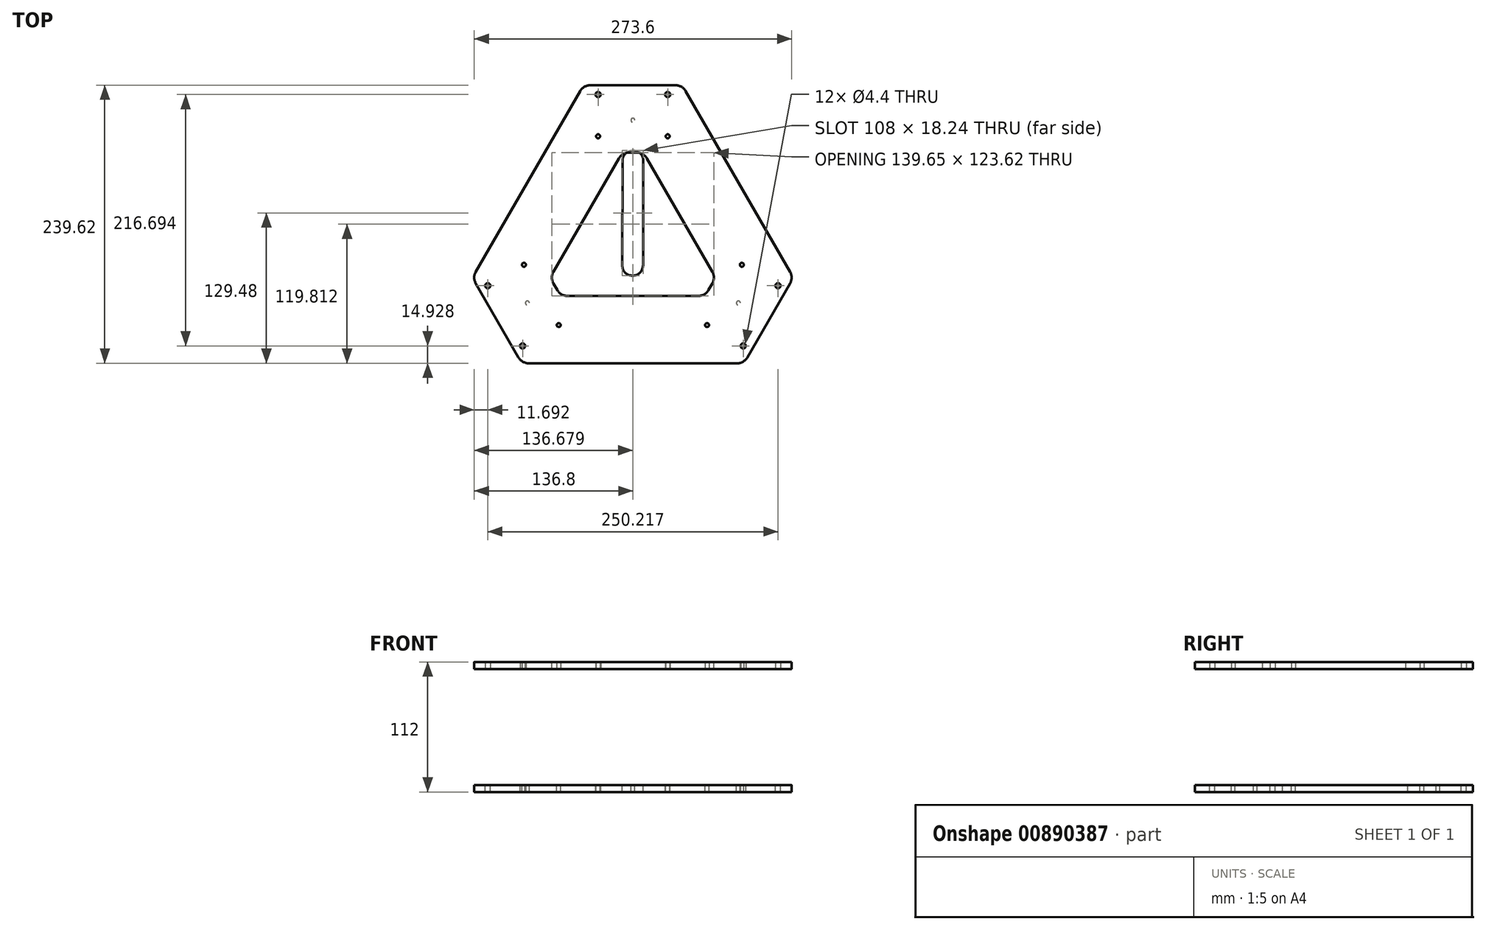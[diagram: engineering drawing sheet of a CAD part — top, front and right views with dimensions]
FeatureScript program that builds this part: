
annotation { "Feature Type Name" : "Feature", "Feature Type Description" : "" }
export const myFeature = defineFeature(function(context is Context, id is Id, definition is map)
    precondition{}
    {
        {
            var Q0;
            Q0=qCreatedBy(makeId("Top.planeOp"),FACE);
            var sketch = newSketch(context, id + "F0", { "sketchPlane" : qUnion([Q0])});
            skLineSegment(sketch, "E0", {"start": v(-138.35, -30.66) * mm, "end": v(-42.62, 135.14) * mm});
            skLineSegment(sketch, "E1", {"start": v(-42.62, 135.14) * mm, "end": v(42.62, 135.14) * mm});
            skLineSegment(sketch, "E2", {"start": v(42.62, 135.14) * mm, "end": v(138.34, -30.66) * mm});
            skLineSegment(sketch, "E3", {"start": v(138.34, -30.66) * mm, "end": v(95.73, -104.48) * mm});
            skLineSegment(sketch, "E4", {"start": v(95.73, -104.48) * mm, "end": v(-95.73, -104.48) * mm});
            skLineSegment(sketch, "E5", {"start": v(-95.73, -104.48) * mm, "end": v(-138.35, -30.66) * mm});
            skLineSegment(sketch, "E6", {"start": v(-90.48, 52.24) * mm, "end": v(0, 0) * mm, "construction": true});
            skLineSegment(sketch, "E7", {"start": v(0, -104.48) * mm, "end": v(0, 0) * mm, "construction": true});
            skLineSegment(sketch, "E8", {"start": v(90.48, 52.24) * mm, "end": v(0, 0) * mm, "construction": true});
            skPoint(sketch, "E9", {"position": v(0, 0) * mm});
            skLineSegment(sketch, "E10.0", {"start": v(62.24, -46.48) * mm, "end": v(-62.24, -46.48) * mm});
            skLineSegment(sketch, "E10.1", {"start": v(-71.37, -30.66) * mm, "end": v(-9.13, 77.14) * mm});
            skLineSegment(sketch, "E10.2", {"start": v(-9.13, 77.14) * mm, "end": v(9.13, 77.14) * mm});
            skLineSegment(sketch, "E10.3", {"start": v(-62.24, -46.48) * mm, "end": v(-71.37, -30.66) * mm});
            skLineSegment(sketch, "E10.4", {"start": v(9.13, 77.14) * mm, "end": v(71.37, -30.66) * mm});
            skLineSegment(sketch, "E10.5", {"start": v(71.37, -30.66) * mm, "end": v(62.24, -46.48) * mm});
            skCircle(sketch, "E11", {"center": v(95.1, -89.55) * mm, "radius": 2.2 * mm});
            skLineSegment(sketch, "E12", {"start": v(117.04, -67.57) * mm, "end": v(66.8, -38.57) * mm, "construction": true});
            skCircle(sketch, "E13", {"center": v(63.93, -71.55) * mm, "radius": 1.7 * mm});
            skCircle(sketch, "E14.MirrorC", {"center": v(93.93, -19.6) * mm, "radius": 1.7 * mm});
            skCircle(sketch, "E15.MirrorC", {"center": v(125.1, -37.6) * mm, "radius": 2.2 * mm});
            skLineSegment(sketch, "E16.0", {"start": v(95.1, -89.55) * mm, "end": v(95.1, -89.55) * mm});
            skLineSegment(sketch, "E16.1", {"start": v(95.1, -89.55) * mm, "end": v(63.93, -71.55) * mm, "construction": true});
            skCircle(sketch, "E17.1.0", {"center": v(-30, 91.14) * mm, "radius": 1.7 * mm});
            skCircle(sketch, "E17.1.1", {"center": v(-30, 127.14) * mm, "radius": 2.2 * mm});
            skCircle(sketch, "E17.1.2", {"center": v(30, 127.14) * mm, "radius": 2.2 * mm});
            skCircle(sketch, "E17.1.3", {"center": v(30, 91.14) * mm, "radius": 1.7 * mm});
            skCircle(sketch, "E17.2.0", {"center": v(-63.93, -71.55) * mm, "radius": 1.7 * mm});
            skCircle(sketch, "E17.2.1", {"center": v(-95.1, -89.55) * mm, "radius": 2.2 * mm});
            skCircle(sketch, "E17.2.2", {"center": v(-125.1, -37.6) * mm, "radius": 2.2 * mm});
            skCircle(sketch, "E17.2.3", {"center": v(-93.93, -19.6) * mm, "radius": 1.7 * mm});
            skSolve(sketch);
        }
        {
            var Q0;
            {var subQ0=sQuery(id+"F0.wireOp",EDGE,"vAaXFV3b-EpbO-ac0L-dCJ6-TkjUisyF59UN");Q0=makeQuery(id+"F0.imprint","IMPRINT",FACE,{"disambiguationData":[TD([[makeQuery(id+"F0.imprint","IMPRINT",EDGE,{"derivedFrom":subQ0}),1.0]])]});}
            var Q1;
            Q1=makeQuery(id+"F0.imprint","IMPRINT",FACE,{"disambiguationData":[TD([[makeQuery(id+"F0.imprint","IMPRINT",EDGE,{"derivedFrom":sQuery(id+"F0.wireOp",EDGE,"E0")}),-1.0]])]});
            extrude(context, id + "F1", {"entities" : qUnion([Q0, Q1]), "depth" : 6 * mm, "offsetDistance" : 25 * mm});
        }
        {
            var Q0;
            Q0=makeQuery(id+"F1.opExtrude","CAP_FACE",FACE,{"disambiguationData":[OSD([sQuery(id+"F0.wireOp",EDGE,"E0"),sQuery(id+"F0.wireOp",EDGE,"E1"),sQuery(id+"F0.wireOp",EDGE,"E2"),sQuery(id+"F0.wireOp",EDGE,"E3"),sQuery(id+"F0.wireOp",EDGE,"E4"),sQuery(id+"F0.wireOp",EDGE,"E5"),sQuery(id+"F0.wireOp",EDGE,"E10.0"),sQuery(id+"F0.wireOp",EDGE,"E10.1"),sQuery(id+"F0.wireOp",EDGE,"E10.2"),sQuery(id+"F0.wireOp",EDGE,"E10.3"),sQuery(id+"F0.wireOp",EDGE,"E10.4"),sQuery(id+"F0.wireOp",EDGE,"E10.5")])],"isStart":true});
            cPlane(context, id + "F2", {"entities" : qUnion([Q0]), "cplaneType" : CPlaneType.OFFSET, "offset" : 100 * mm, "width" : 150 * mm, "height" : 150 * mm});
        }
        {
            var Q0;
            Q0=qCreatedBy(id+"F2.planeOp",FACE);
            var sketch = newSketch(context, id + "F3", { "sketchPlane" : qUnion([Q0])});
            skLineSegment(sketch, "E18", {"start": v(-95.73, 104.48) * mm, "end": v(95.73, 104.48) * mm});
            skLineSegment(sketch, "E19", {"start": v(95.73, 104.48) * mm, "end": v(138.35, 30.66) * mm});
            skLineSegment(sketch, "E20", {"start": v(138.35, 30.66) * mm, "end": v(42.62, -135.14) * mm});
            skLineSegment(sketch, "E21", {"start": v(42.62, -135.14) * mm, "end": v(-42.62, -135.14) * mm});
            skLineSegment(sketch, "E22", {"start": v(-42.62, -135.14) * mm, "end": v(-138.34, 30.66) * mm});
            skLineSegment(sketch, "E23", {"start": v(-138.34, 30.66) * mm, "end": v(-95.73, 104.48) * mm});
            skPoint(sketch, "E24", {"position": v(0, 0) * mm});
            skCircle(sketch, "E25", {"center": v(-30, -127.14) * mm, "radius": 2.2 * mm});
            skLineSegment(sketch, "E26", {"start": v(0, -275.74) * mm, "end": v(0, -135.14) * mm, "construction": true});
            skCircle(sketch, "E27", {"center": v(-30, -91.14) * mm, "radius": 1.7 * mm});
            skCircle(sketch, "E28.MirrorC", {"center": v(30, -91.14) * mm, "radius": 1.7 * mm});
            skCircle(sketch, "E29.MirrorC", {"center": v(30, -127.14) * mm, "radius": 2.2 * mm});
            skLineSegment(sketch, "E30.1", {"start": v(-30, -127.14) * mm, "end": v(-30, -91.14) * mm, "construction": true});
            skCircle(sketch, "E31.1.0", {"center": v(125.1, 37.6) * mm, "radius": 2.2 * mm});
            skCircle(sketch, "E31.1.1", {"center": v(93.93, 19.6) * mm, "radius": 1.7 * mm});
            skCircle(sketch, "E31.1.2", {"center": v(63.93, 71.55) * mm, "radius": 1.7 * mm});
            skCircle(sketch, "E31.1.3", {"center": v(95.1, 89.55) * mm, "radius": 2.2 * mm});
            skCircle(sketch, "E31.2.0", {"center": v(-95.1, 89.55) * mm, "radius": 2.2 * mm});
            skCircle(sketch, "E31.2.1", {"center": v(-63.93, 71.55) * mm, "radius": 1.7 * mm});
            skCircle(sketch, "E31.2.2", {"center": v(-93.93, 19.6) * mm, "radius": 1.7 * mm});
            skCircle(sketch, "E31.2.3", {"center": v(-125.1, 37.6) * mm, "radius": 2.2 * mm});
            skLineSegment(sketch, "E32", {"start": v(0, -70) * mm, "end": v(-0.24, 20) * mm, "construction": true});
            skArc(sketch, "E33.0.startCap", {"start": v(9, -69.98) * mm, "mid": v(0.02, -79) * mm, "end": v(-9, -70.02) * mm});
            skArc(sketch, "E33.0.endCap", {"start": v(-9.24, 19.98) * mm, "mid": v(-0.27, 29) * mm, "end": v(8.76, 20.02) * mm});
            skLineSegment(sketch, "E33.0.left", {"start": v(-9, -70.02) * mm, "end": v(-9.24, 19.98) * mm});
            skLineSegment(sketch, "E33.0.right", {"start": v(9, -69.98) * mm, "end": v(8.76, 20.02) * mm});
            skCircle(sketch, "E34", {"center": v(0, 0) * mm, "radius": 110 * mm, "construction": true});
            skCircle(sketch, "E35", {"center": v(0, -105) * mm, "radius": 1.7 * mm});
            skCircle(sketch, "E36.1.0", {"center": v(90.93, 52.5) * mm, "radius": 1.7 * mm});
            skCircle(sketch, "E36.2.0", {"center": v(-90.93, 52.5) * mm, "radius": 1.7 * mm});
            skLineSegment(sketch, "E37", {"start": v(-90.48, -52.24) * mm, "end": v(0, 0) * mm, "construction": true});
            skLineSegment(sketch, "E38", {"start": v(90.48, -52.24) * mm, "end": v(0, 0) * mm, "construction": true});
            skLineSegment(sketch, "E39", {"start": v(0, 104.48) * mm, "end": v(0, 0) * mm, "construction": true});
            skSolve(sketch);
        }
        {
            var Q0;
            Q0=qSketchRegion(id+"F3",true);
            extrude(context, id + "F4", {"entities" : qUnion([Q0]), "depth" : 6 * mm, "offsetDistance" : 25 * mm});
        }
        {
            var Q0;
            Q0=makeQuery(id+"F1.opExtrude","SWEPT_EDGE",EDGE,{"disambiguationData":[OSD([sQuery(id+"F0.wireOp",EDGE,"E4"),sQuery(id+"F0.wireOp",EDGE,"E5")])]});
            var Q1;
            Q1=makeQuery(id+"F1.opExtrude","SWEPT_EDGE",EDGE,{"disambiguationData":[OSD([sQuery(id+"F0.wireOp",EDGE,"E0"),sQuery(id+"F0.wireOp",EDGE,"E5")])]});
            var Q2;
            Q2=makeQuery(id+"F1.opExtrude","SWEPT_EDGE",EDGE,{"disambiguationData":[OSD([sQuery(id+"F0.wireOp",EDGE,"E3"),sQuery(id+"F0.wireOp",EDGE,"E4")])]});
            var Q3;
            Q3=makeQuery(id+"F1.opExtrude","SWEPT_EDGE",EDGE,{"disambiguationData":[OSD([sQuery(id+"F0.wireOp",EDGE,"E2"),sQuery(id+"F0.wireOp",EDGE,"E3")])]});
            var Q4;
            Q4=makeQuery(id+"F1.opExtrude","SWEPT_EDGE",EDGE,{"disambiguationData":[OSD([sQuery(id+"F0.wireOp",EDGE,"E0"),sQuery(id+"F0.wireOp",EDGE,"E1")])]});
            var Q5;
            Q5=makeQuery(id+"F1.opExtrude","SWEPT_EDGE",EDGE,{"disambiguationData":[OSD([sQuery(id+"F0.wireOp",EDGE,"E1"),sQuery(id+"F0.wireOp",EDGE,"E2")])]});
            var Q6;
            Q6=makeQuery(id+"F1.opExtrude","SWEPT_EDGE",EDGE,{"disambiguationData":[OSD([sQuery(id+"F0.wireOp",EDGE,"E10.1"),sQuery(id+"F0.wireOp",EDGE,"E10.3")])]});
            var Q7;
            Q7=makeQuery(id+"F1.opExtrude","SWEPT_EDGE",EDGE,{"disambiguationData":[OSD([sQuery(id+"F0.wireOp",EDGE,"E10.0"),sQuery(id+"F0.wireOp",EDGE,"E10.3")])]});
            var Q8;
            Q8=makeQuery(id+"F1.opExtrude","SWEPT_EDGE",EDGE,{"disambiguationData":[OSD([sQuery(id+"F0.wireOp",EDGE,"E10.1"),sQuery(id+"F0.wireOp",EDGE,"E10.2")])]});
            var Q9;
            Q9=makeQuery(id+"F1.opExtrude","SWEPT_EDGE",EDGE,{"disambiguationData":[OSD([sQuery(id+"F0.wireOp",EDGE,"E10.2"),sQuery(id+"F0.wireOp",EDGE,"E10.4")])]});
            var Q10;
            Q10=makeQuery(id+"F1.opExtrude","SWEPT_EDGE",EDGE,{"disambiguationData":[OSD([sQuery(id+"F0.wireOp",EDGE,"E10.4"),sQuery(id+"F0.wireOp",EDGE,"E10.5")])]});
            var Q11;
            Q11=makeQuery(id+"F1.opExtrude","SWEPT_EDGE",EDGE,{"disambiguationData":[OSD([sQuery(id+"F0.wireOp",EDGE,"E10.0"),sQuery(id+"F0.wireOp",EDGE,"E10.5")])]});
            var Q12;
            Q12=makeQuery(id+"F4.opExtrude","SWEPT_EDGE",EDGE,{"disambiguationData":[OSD([sQuery(id+"F3.wireOp",EDGE,"E18"),sQuery(id+"F3.wireOp",EDGE,"E19")])]});
            var Q13;
            Q13=makeQuery(id+"F4.opExtrude","SWEPT_EDGE",EDGE,{"disambiguationData":[OSD([sQuery(id+"F3.wireOp",EDGE,"E19"),sQuery(id+"F3.wireOp",EDGE,"E20")])]});
            var Q14;
            Q14=makeQuery(id+"F4.opExtrude","SWEPT_EDGE",EDGE,{"disambiguationData":[OSD([sQuery(id+"F3.wireOp",EDGE,"E18"),sQuery(id+"F3.wireOp",EDGE,"E23")])]});
            var Q15;
            Q15=makeQuery(id+"F4.opExtrude","SWEPT_EDGE",EDGE,{"disambiguationData":[OSD([sQuery(id+"F3.wireOp",EDGE,"E22"),sQuery(id+"F3.wireOp",EDGE,"E23")])]});
            var Q16;
            Q16=makeQuery(id+"F4.opExtrude","SWEPT_EDGE",EDGE,{"disambiguationData":[OSD([sQuery(id+"F3.wireOp",EDGE,"E21"),sQuery(id+"F3.wireOp",EDGE,"E22")])]});
            var Q17;
            Q17=makeQuery(id+"F4.opExtrude","SWEPT_EDGE",EDGE,{"disambiguationData":[OSD([sQuery(id+"F3.wireOp",EDGE,"E20"),sQuery(id+"F3.wireOp",EDGE,"E21")])]});
            fillet(context, id + "F5", {"entities" : qUnion([Q0, Q1, Q2, Q3, Q4, Q5, Q6, Q7, Q8, Q9, Q10, Q11, Q12, Q13, Q14, Q15, Q16, Q17]), "radius" : 10 * mm, "tangentPropagation" : true, "allowEdgeOverflow" : false});
        }
    });
